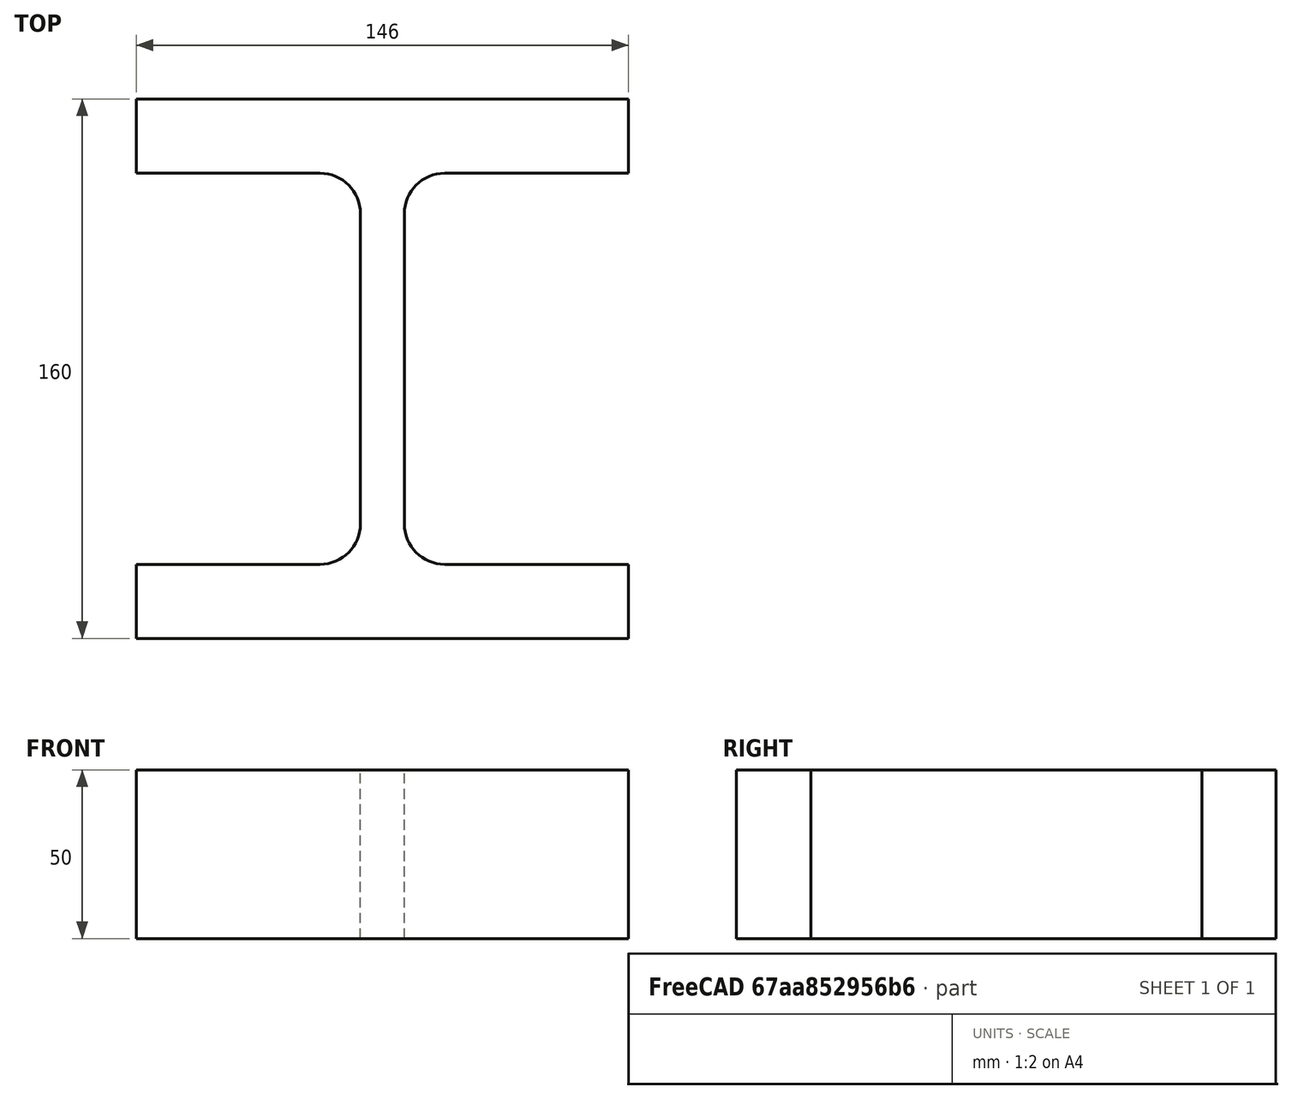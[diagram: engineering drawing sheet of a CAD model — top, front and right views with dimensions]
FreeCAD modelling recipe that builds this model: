
FCSTD DOCUMENT  (FreeCAD 0.15R4671 (Git))
Label: HE-M-Profile 140 DIN1025-4 S235JR
License: All rights reserved
LicenseURL: http://en.wikipedia.org/wiki/All_rights_reserved
objects: Sketcher::SketchObject×1, Part::Extrusion×1
note: 2 computed .brp shape members not serialized (recipe doc carries the construction recipe); baked Part::Feature solids carry a one-line shape summary decoded from their .brp

FEATURE [Sketcher::SketchObject] Sketch
  sketch-geometry (16):
    g0: LineSegment StartX=6.5 StartY=-46 StartZ=0 EndX=6.5 EndY=46 EndZ=0
    g1: LineSegment StartX=18.5 StartY=58 StartZ=0 EndX=73 EndY=58 EndZ=0
    g2: LineSegment StartX=73 StartY=58 StartZ=0 EndX=73 EndY=80 EndZ=0
    g3: LineSegment StartX=73 StartY=80 StartZ=0 EndX=-73 EndY=80 EndZ=0
    g4: LineSegment StartX=-73 StartY=80 StartZ=0 EndX=-73 EndY=58 EndZ=0
    g5: LineSegment StartX=-73 StartY=58 StartZ=0 EndX=-18.5 EndY=58 EndZ=0
    g6: LineSegment StartX=-6.5 StartY=46 StartZ=0 EndX=-6.5 EndY=-46 EndZ=0
    g7: LineSegment StartX=-18.5 StartY=-58 StartZ=0 EndX=-73 EndY=-58 EndZ=0
    g8: LineSegment StartX=-73 StartY=-58 StartZ=0 EndX=-73 EndY=-80 EndZ=0
    g9: LineSegment StartX=-73 StartY=-80 StartZ=0 EndX=73 EndY=-80 EndZ=0
    g10: LineSegment StartX=73 StartY=-80 StartZ=0 EndX=73 EndY=-58 EndZ=0
    g11: LineSegment StartX=73 StartY=-58 StartZ=0 EndX=18.5 EndY=-58 EndZ=0
    g12: ArcOfCircle CenterX=18.5 CenterY=46 CenterZ=0 NormalX=0 NormalY=0 NormalZ=1 Radius=12 StartAngle=1.5708 EndAngle=3.14159
    g13: ArcOfCircle CenterX=18.5 CenterY=-46 CenterZ=0 NormalX=0 NormalY=0 NormalZ=1 Radius=12 StartAngle=3.14159 EndAngle=4.71239
    g14: ArcOfCircle CenterX=-18.5 CenterY=46 CenterZ=0 NormalX=0 NormalY=0 NormalZ=1 Radius=12 StartAngle=0 EndAngle=1.5708
    g15: ArcOfCircle CenterX=-18.5 CenterY=-46 CenterZ=0 NormalX=0 NormalY=0 NormalZ=1 Radius=12 StartAngle=4.71239 EndAngle=6.28319
  constraints (42):
    c: Vertical(g0)
    c: Coincident(g2,g1)
    c: Vertical(g2)
    c: Coincident(g3,g2)
    c: Coincident(g4,g3)
    c: Vertical(g4)
    c: Coincident(g5,g4)
    c: Horizontal(g5)
    c: Vertical(g6)
    c: Horizontal(g7)
    c: Coincident(g8,g7)
    c: Vertical(g8)
    c: Coincident(g9,g8)
    c: Horizontal(g9)
    c: Coincident(g10,g9)
    c: Vertical(g10)
    c: Coincident(g11,g10)
    c: Horizontal(g11)
    c: Tangent(g1,g12) = 1.5708
    c: Tangent(g0,g12) = 1.5708
    c: Tangent(g0,g13) = 1.5708
    c: Tangent(g11,g13) = 1.5708
    c: Tangent(g5,g14) = 1.5708
    c: Tangent(g6,g14) = 1.5708
    c: Tangent(g6,g15) = 1.5708
    c: Tangent(g7,g15) = 1.5708
    c: Equal(g3,g9)
    c: Equal(g2,g4)
    c: Equal(g4,g8)
    c: Equal(g8,g10)
    c: Equal(g12,g14)
    c: Equal(g14,g15)
    c: Equal(g15,g13)
    c: Symmetric(g2,g3,g-2)
    c: Symmetric(g9,g8,g-2)
    c: Symmetric(g0,g6,g-2)
    c: Symmetric(g2,g9,g-1)
    c: DistanceY(g2,g9) = -160
    c: DistanceX(g3) = -146
    c: DistanceX(g0,g6) = -13
    c: DistanceY(g2) = 22
    c: Radius(g12) = 12
FEATURE [Part::Extrusion] Extrude  label="HE-M-Profile 140 DIN1025-4 S235JR"
  Base = -> Sketch
  Dir = (0,0,50)
  Solid = true
